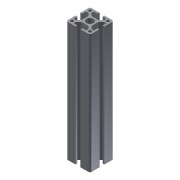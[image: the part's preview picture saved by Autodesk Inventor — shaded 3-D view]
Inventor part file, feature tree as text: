
AUTODESK INVENTOR PART (.ipt)
format: ipt  version: 2016 (Build 200138000, 138)  size: 186,368 bytes
history: native  units: mm
features: other x42, sketch x5, hole x4, extrude x1
ambient origin geometry x8: Origin, YZ Plane, XZ Plane, XY Plane, X Axis, Y Axis, Z Axis, Center Point
bodies: Solid1 (feature_tree)
feature tree (52):
  extrude  "Extrusion1"  [1 undecoded]
  hole  "Drilling 1"  [1 undecoded]
  hole  "Drilling 2"  [1 undecoded]
  hole  "Drilling 3"  [1 undecoded]
  hole  "Drilling 4"  [1 undecoded]
  other  "side_4d_XY"
  other  "side_4d_YZ"
  other  "side_4d_ZX"
  other  "side_4d_X"
  other  "side_4d_Y"
  other  "side_4d_Z"
  other  "side_4d_Center"
  other  "side_1a_XY"
  other  "side_1a_YZ"
  other  "side_1a_ZX"
  other  "side_1a_X"
  other  "side_1a_Y"
  other  "side_1a_Z"
  other  "side_1a_Center"
  other  "side_2b_XY"
  other  "side_2b_YZ"
  other  "side_2b_ZX"
  other  "side_2b_X"
  other  "side_2b_Y"
  other  "side_2b_Z"
  other  "side_2b_Center"
  other  "side_3c_XY"
  other  "side_3c_YZ"
  other  "side_3c_ZX"
  other  "side_3c_X"
  other  "side_3c_Y"
  other  "side_3c_Z"
  other  "side_3c_Center"
  other  "end_XY"
  other  "end_YZ"
  other  "end_ZX"
  other  "end_X"
  other  "end_Y"
  other  "end_Z"
  other  "end_Center"
  other  "start_XY"
  other  "start_YZ"
  other  "start_ZX"
  other  "start_X"
  other  "start_Y"
  other  "start_Z"
  other  "start_Center"
  sketch  "Skizze_1"  dims[d0=200.0mm d1=0.0mm]
  sketch  "Sketch2"  dims[d2=5.0mm d3=6.0mm d4=4.0mm d5=2.0mm d6=90.0deg d7=6000.0mm d8=0.0mm]
  sketch  "Sketch3"  dims[d9=5.0mm d10=6.0mm d11=4.0mm d12=2.0mm d13=90.0deg d14=6000.0mm d15=0.0mm]
  sketch  "Sketch4"  dims[d16=5.0mm d17=6.0mm d18=4.0mm d19=2.0mm d20=90.0deg d21=6000.0mm d22=0.0mm]
  sketch  "Sketch5"  dims[d23=5.0mm d24=6.0mm d25=4.0mm d26=2.0mm d27=90.0deg d28=6000.0mm d29=0.0mm]
note: 5 required parameter values undecoded (feature->parameter linkage not recoverable at this tier; creation-order binding heuristic only, values carry confidence <= 0.55)
